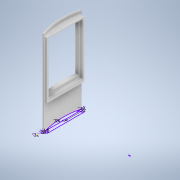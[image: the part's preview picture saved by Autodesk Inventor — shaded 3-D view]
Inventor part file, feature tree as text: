
AUTODESK INVENTOR PART (.ipt)
format: ipt  version: 2022 (Build 260153000, 153)  size: 164,864 bytes
history: native  units: mm
features: extrude x8, sketch x1
ambient origin geometry x8: Origin, YZ Plane, XZ Plane, XY Plane, X Axis, Y Axis, Z Axis, Center Point
bodies: Body1 (feature_tree)
feature tree (9):
  sketch  "Sketch1"  dims[d1=2.0mm d3=2.0mm d4=2.0mm d5=2.0mm d6=32.0mm d8=3.6mm d9=2.0mm d10=2.5mm d11=2.0mm d12=5.0mm d29=1.7mm d37=138.0mm d38=0.0mm d39=133.0mm d40=0.0mm d41=133.0mm d42=0.0mm d43=131.0mm d44=0.0mm d45=129.0mm d46=0.0mm d47=51.0mm d48=0.0mm d49=47.0mm d50=0.0mm d53=42.0mm d54=0.0mm]
  extrude  "Extrusion12"  Depth=42.0mm
  extrude  "Extrusion13"  Depth=2.0mm
  extrude  "Extrusion14"  Depth=42.0mm
  extrude  "Extrusion15"  Depth=2.0mm
  extrude  "Extrusion16"  Depth=5.0mm
  extrude  "Extrusion17"  Depth=1.7mm
  extrude  "Extrusion18"  Depth=138.0mm TaperAngle=0.0deg
  extrude  "Extrusion20"  Depth=133.0mm TaperAngle=0.0deg
